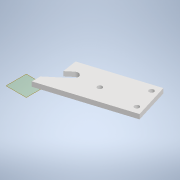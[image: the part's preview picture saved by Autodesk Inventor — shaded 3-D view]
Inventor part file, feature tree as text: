
AUTODESK INVENTOR PART (.ipt)
format: ipt  version: 2022 (Build 260153000, 153)  size: 124,416 bytes
history: native  units: mm
features: other x1, extrude x1, sketch x1
ambient origin geometry x8: Origin, YZ Plane, XZ Plane, XY Plane, X Axis, Y Axis, Z Axis, Center Point
bodies: Body1 (feature_tree)
feature tree (3):
  other  "РабПлоскость1"
  extrude  "Выдавливание1"  Depth=5.0mm TaperAngle=0.0deg
  sketch  "Эскиз1"
